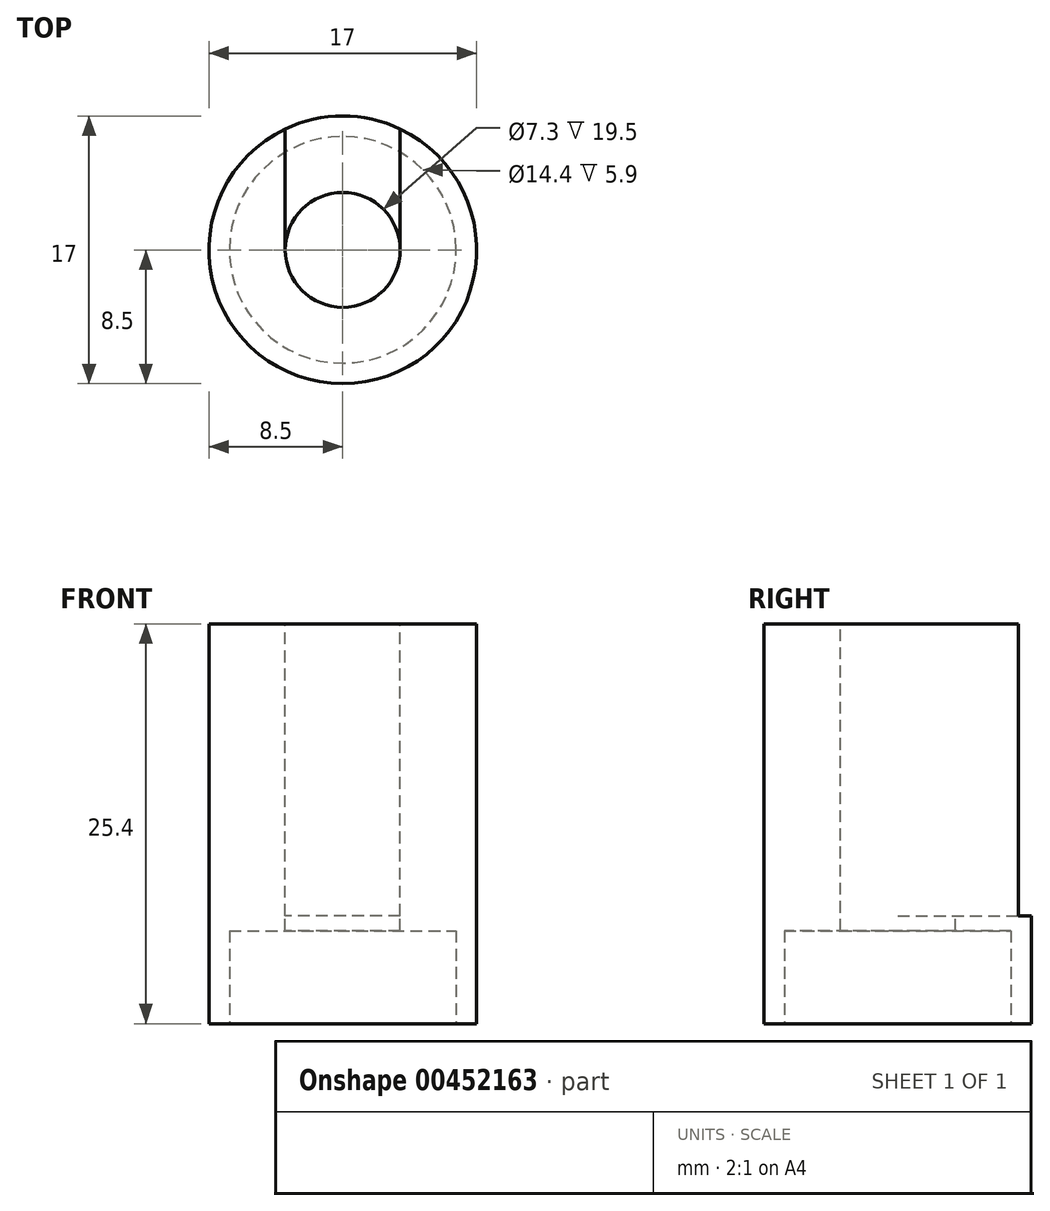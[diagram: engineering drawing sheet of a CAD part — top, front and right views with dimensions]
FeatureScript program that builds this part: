
annotation { "Feature Type Name" : "Feature", "Feature Type Description" : "" }
export const myFeature = defineFeature(function(context is Context, id is Id, definition is map)
    precondition{}
    {
        {
            var Q0;
            Q0=qCreatedBy(makeId("Top.planeOp"),FACE);
            var sketch = newSketch(context, id + "F0", { "sketchPlane" : qUnion([Q0])});
            skCircle(sketch, "E0", {"center": v(0, 0) * mm, "radius": 8.5 * mm});
            skSolve(sketch);
        }
        {
            var Q0;
            Q0=makeQuery(id+"F0.imprint","IMPRINT",FACE,{"disambiguationData":[TD([[makeQuery(id+"F0.imprint","IMPRINT",EDGE,{"derivedFrom":sQuery(id+"F0.wireOp",EDGE,"E0")}),1.0]])]});
            extrude(context, id + "F1", {"entities" : qUnion([Q0]), "depth" : 25.4 * mm});
        }
        {
            var Q0;
            Q0=makeQuery(id+"F1.opExtrude","CAP_FACE",FACE,{"disambiguationData":[OSD([sQuery(id+"F0.wireOp",EDGE,"E0")])],"isStart":false});
            var sketch = newSketch(context, id + "F2", { "sketchPlane" : qUnion([Q0])});
            skPoint(sketch, "E1", {"position": v(0, 0) * mm});
            skSolve(sketch);
        }
        {
            var Q0;
            Q0=sQuery(id+"F2.wireOp",VERTEX,"E1");
            var Q1;
            Q1=makeQuery(id+"F1.opExtrude","SWEPT_BODY",BODY,{"disambiguationData":[OSD([sQuery(id+"F0.wireOp",EDGE,"E0")])]});
            hole(context, id + "F3", {"style" : HoleStyle.SIMPLE, "endStyle" : HoleEndStyle.THROUGH, "holeDiameter" : 7.3 * mm, "isTappedThrough" : true, "tappedDepth" : 12.7 * mm, "tapClearance" : 3, "locations" : qUnion([Q0]), "scope" : qUnion([Q1])});
        }
        {
            var Q0;
            Q0=makeQuery(id+"F1.opExtrude","CAP_FACE",FACE,{"disambiguationData":[OSD([sQuery(id+"F0.wireOp",EDGE,"E0")])],"isStart":false});
            var sketch = newSketch(context, id + "F4", { "sketchPlane" : qUnion([Q0])});
            skLineSegment(sketch, "E2", {"start": v(-3.65, 0) * mm, "end": v(-3.65, 7.68) * mm});
            skLineSegment(sketch, "E3", {"start": v(3.65, 0) * mm, "end": v(3.65, 7.68) * mm});
            skSolve(sketch);
        }
        {
            var Q0;
            {var subQ0=sQuery(id+"F4.wireOp",EDGE,"E2");Q0=makeQuery(id+"F4.imprint","IMPRINT",FACE,{"disambiguationData":[TD([[makeQuery(id+"F4.imprint","IMPRINT",EDGE,{"derivedFrom":subQ0}),-1.0]])]});}
            extrude(context, id + "F5", {"entities" : qUnion([Q0]), "operationType" : NewBodyOperationType.REMOVE, "oppositeDirection" : true, "depth" : 18.54 * mm});
        }
        {
            var Q0;
            Q0=makeQuery(id+"F1.opExtrude","CAP_FACE",FACE,{"disambiguationData":[OSD([sQuery(id+"F0.wireOp",EDGE,"E0")])],"isStart":true});
            var sketch = newSketch(context, id + "F6", { "sketchPlane" : qUnion([Q0])});
            skCircle(sketch, "E4", {"center": v(0, 0) * mm, "radius": 7.2 * mm});
            skSolve(sketch);
        }
        {
            var Q0;
            Q0=makeQuery(id+"F6.imprint","IMPRINT",FACE,{"disambiguationData":[TD([[makeQuery(id+"F6.imprint","IMPRINT",EDGE,{"derivedFrom":sQuery(id+"F6.wireOp",EDGE,"E4")}),1.0]])]});
            extrude(context, id + "F7", {"entities" : qUnion([Q0]), "operationType" : NewBodyOperationType.REMOVE, "oppositeDirection" : true, "depth" : 5.9 * mm});
        }
    });
